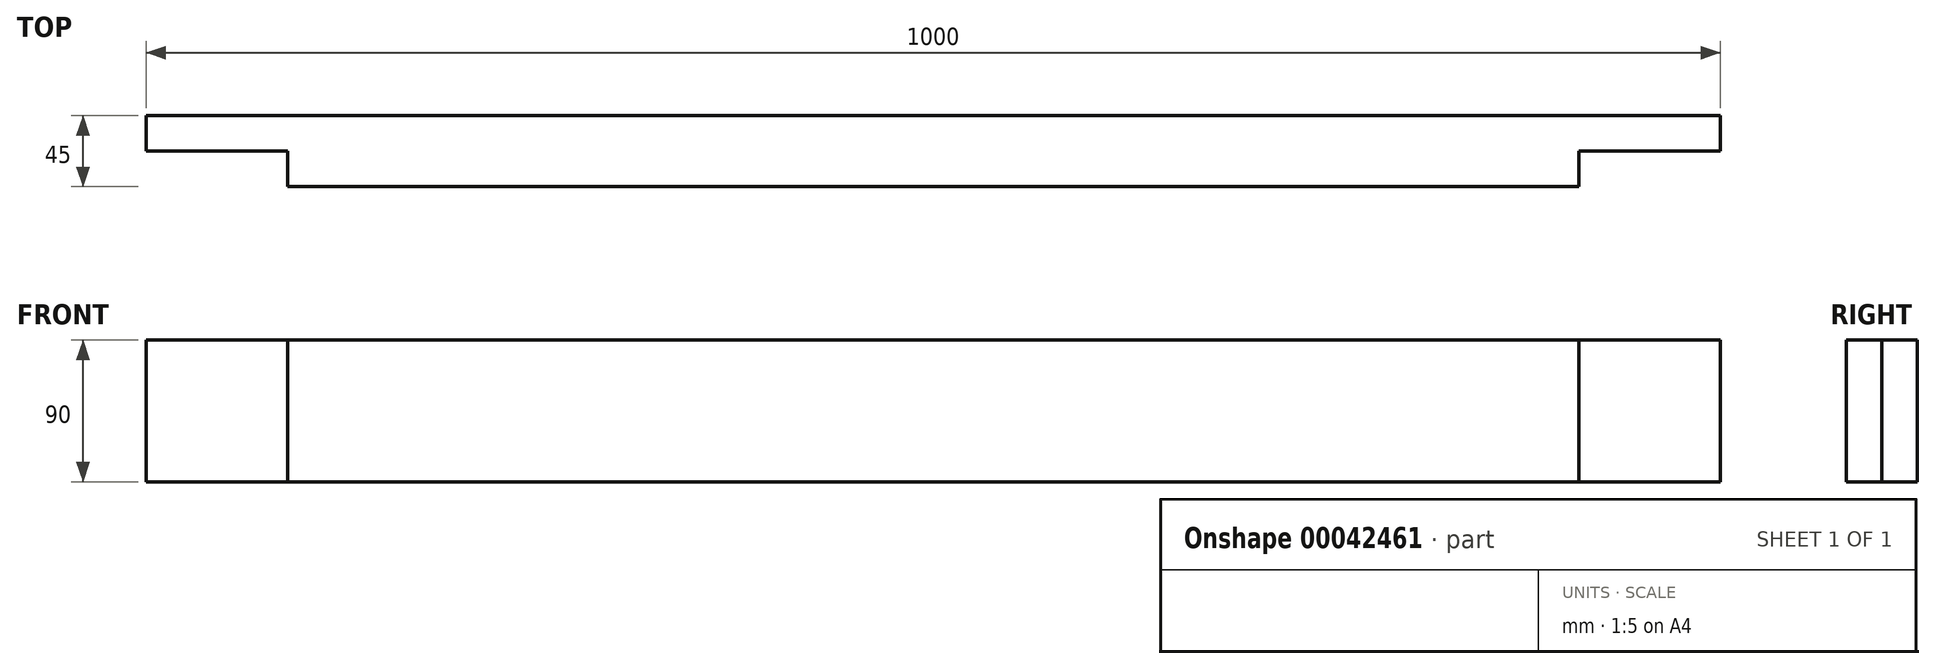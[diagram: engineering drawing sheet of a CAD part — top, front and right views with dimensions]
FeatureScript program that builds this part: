
annotation { "Feature Type Name" : "Feature", "Feature Type Description" : "" }
export const myFeature = defineFeature(function(context is Context, id is Id, definition is map)
    precondition{}
    {
        {
            assignVariable(context, id + "F0", {"name" : "depth", "anyValue" : 45});
        }
        {
            var Q0;
            Q0=qCreatedBy(makeId("Front.planeOp"),FACE);
            var sketch = newSketch(context, id + "F1", { "sketchPlane" : qUnion([Q0])});
            skLineSegment(sketch, "E0.bottom", {"start": v(0, 0) * mm, "end": v(1000, 0) * mm});
            skLineSegment(sketch, "E0.top", {"start": v(0, 90) * mm, "end": v(1000, 90) * mm});
            skLineSegment(sketch, "E0.left", {"start": v(0, 0) * mm, "end": v(0, 90) * mm});
            skLineSegment(sketch, "E0.right", {"start": v(1000, 0) * mm, "end": v(1000, 90) * mm});
            skSolve(sketch);
        }
        {
            var Q0;
            Q0 = qSketchRegion(id + "F1", true);
            extrude(context, id + "F2", {"entities" : qUnion([Q0]), "depth" : (getVariable(context, 'depth')) * mm});
        }
        {
            var Q0;
            Q0=makeQuery(id+"F2.opExtrude","CAP_FACE",FACE,{"disambiguationData":[OSD([sQuery(id+"F1.wireOp",EDGE,"E0.bottom"),sQuery(id+"F1.wireOp",EDGE,"E0.top"),sQuery(id+"F1.wireOp",EDGE,"E0.left"),sQuery(id+"F1.wireOp",EDGE,"E0.right")])],"isStart":false});
            var sketch = newSketch(context, id + "F3", { "sketchPlane" : qUnion([Q0])});
            skLineSegment(sketch, "E1.bottom", {"start": v(0, 90) * mm, "end": v(90, 90) * mm});
            skLineSegment(sketch, "E1.top", {"start": v(0, 0) * mm, "end": v(90, 0) * mm});
            skLineSegment(sketch, "E1.left", {"start": v(0, 90) * mm, "end": v(0, 0) * mm});
            skLineSegment(sketch, "E1.right", {"start": v(90, 90) * mm, "end": v(90, 0) * mm});
            skLineSegment(sketch, "E2.bottom", {"start": v(1000, 90) * mm, "end": v(910, 90) * mm});
            skLineSegment(sketch, "E2.top", {"start": v(1000, 0) * mm, "end": v(910, 0) * mm});
            skLineSegment(sketch, "E2.left", {"start": v(1000, 90) * mm, "end": v(1000, 0) * mm});
            skLineSegment(sketch, "E2.right", {"start": v(910, 90) * mm, "end": v(910, 0) * mm});
            skSolve(sketch);
        }
        {
            var Q0;
            Q0 = qSketchRegion(id + "F3", true);
            extrude(context, id + "F4", {"entities" : qUnion([Q0]), "operationType" : NewBodyOperationType.REMOVE, "oppositeDirection" : true, "depth" : (getVariable(context, 'depth') / 2) * mm});
        }
    });
